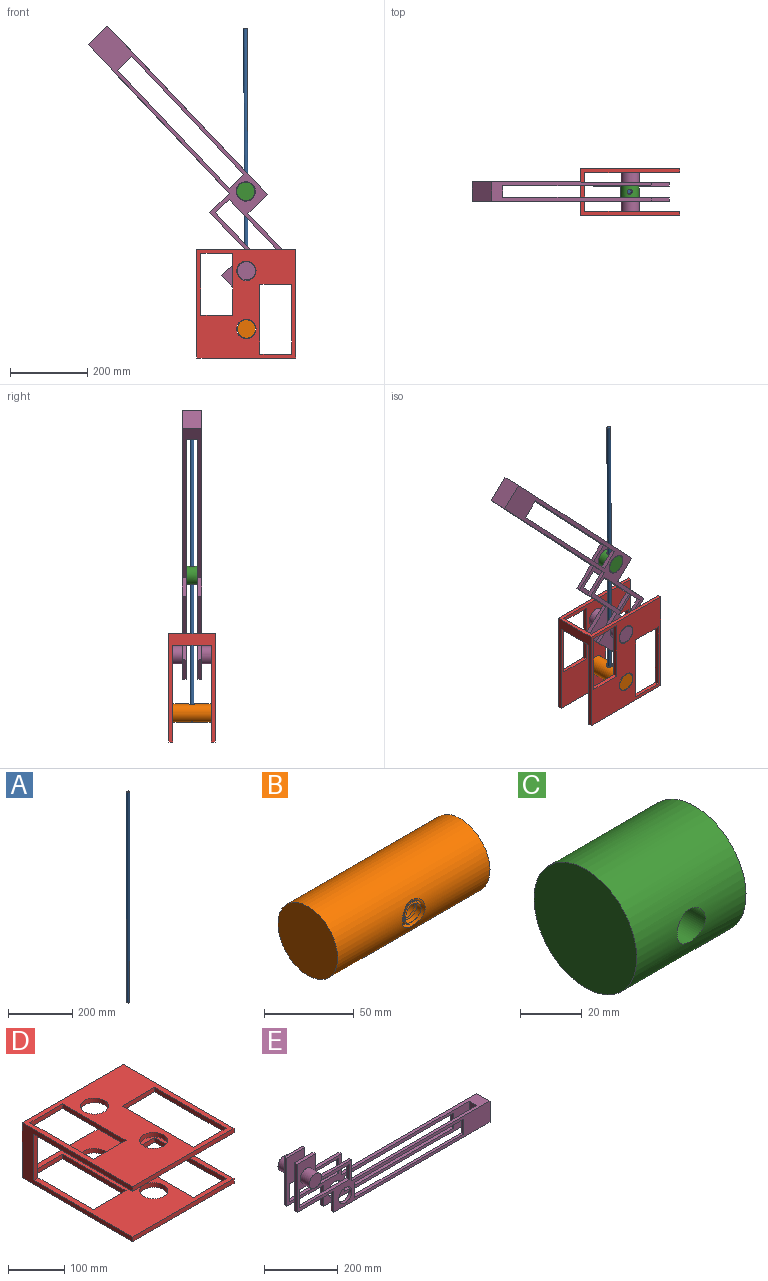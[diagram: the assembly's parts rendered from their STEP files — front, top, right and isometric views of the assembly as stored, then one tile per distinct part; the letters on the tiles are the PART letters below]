
ASSEMBLY  parts=5 mates=5
PART A: 3 faces, bbox 10x10x800 mm
  f0: cylinder r=5mm len=800mm, axis (0,0,-1), area 25132.7mm2, adj f1,f2
  f1: plane 10x10mm, normal (0,0,1), area 78.5mm2, adj f0
  f2: plane 10x10mm, normal (0,0,-1), area 78.5mm2, adj f0
PART B: 18 faces, bbox 120x48.7x47 mm
  f0: cylinder r=23.5mm len=120mm, axis (-1,0,0), area 17326.1mm2, adj f1,f11,f12,f13
  f1: cylinder r=6.5mm len=13mm, axis (0,1,0), area 373.7mm2, adj f0,f2,f14,f15,f16
  f2: cylinder r=6.5mm len=13mm, axis (0,1,0), area 132.8mm2, adj f1,f3,f15,f16
  f3: cylinder r=6.5mm len=13mm, axis (0,1,0), area 132.8mm2, adj f2,f4,f15,f16
  f4: cylinder r=6.5mm len=13mm, axis (0,1,0), area 132.8mm2, adj f3,f5,f15,f16
  f5: cylinder r=6.5mm len=13mm, axis (0,1,0), area 132.8mm2, adj f4,f6,f15,f16
  f6: cylinder r=6.5mm len=13mm, axis (0,1,0), area 132.8mm2, adj f5,f7,f15,f16
  f7: cylinder r=6.5mm len=13mm, axis (0,1,0), area 132.8mm2, adj f6,f8,f15,f16
  f8: cylinder r=6.5mm len=13mm, axis (0,1,0), area 129.1mm2, adj f7,f9,f10,f15,f16
  f9: cylinder r=6.5mm len=12.36mm, axis (0,1,0), area 17.2mm2, adj f8,f10,f16
  f10: cylinder r=23.5mm len=13.46mm, axis (-1,0,0), area 23.3mm2, adj f8,f9,f15,f16
  f11: plane 47x47mm, normal (1,0,0), area 1734.9mm2, adj f0
  f12: plane 47x47mm, normal (-1,0,0), area 1734.9mm2, adj f0
  f13: cylinder r=8.98mm len=41.22mm, axis (0,1,0), area 2185.7mm2, adj f0,f14,f17
  f14: plane 6.01x3.66mm, normal (0.6,0,0.8), area 18.2mm2, adj f1,f13,f15,f16,f17
  f15: bspline ~42.41x15.26mm, area 691mm2, adj f1,f2,f3,f4,f5,f6,f7,f8
  f16: bspline ~41.67x17.79mm, area 766.8mm2, adj f1,f2,f3,f4,f5,f6,f7,f8
  f17: bspline ~20.58x19.11mm, area 77mm2, adj f13,f14,f15
PART C: 4 faces, bbox 50x47x47 mm
  f0: cylinder r=23.5mm len=50mm, axis (1,0,0), area 7114.4mm2, adj f1,f2,f3
  f1: plane 47x47mm, normal (-1,0,0), area 1734.9mm2, adj f0
  f2: cylinder r=6.5mm len=47mm, axis (0,1,0), area 1882.3mm2, adj f0
  f3: plane 47x47mm, normal (1,0,0), area 1734.9mm2, adj f0
PART D: 32 faces, bbox 255x280x120 mm
  f0: plane 280x255mm, normal (0,0,1), area 39423mm2, adj f4,f5,f6,f7,f11,f12,f16,f17
  f1: plane 280x255mm, normal (0,0,-1), area 39423mm2, adj f6,f7,f8,f9,f13,f14,f24,f25
  f2: plane 280x255mm, normal (0,0,1), area 39129mm2, adj f6,f7,f8,f9,f10,f13,f14,f15
  f3: plane 280x255mm, normal (0,0,-1), area 39129mm2, adj f4,f5,f6,f7,f10,f11,f12,f15
  f4: plane 255x10mm, normal (0,-1,0), area 2550mm2, adj f0,f3,f5,f7
  f5: plane 280x10mm, normal (1,0,0), area 2800mm2, adj f0,f3,f4,f6
  f6: plane 255x120mm, normal (0,1,0), area 6080mm2, adj f0,f1,f2,f3,f5,f7,f9,f10
  f7: plane 280x120mm, normal (-1,0,0), area 8600mm2, adj f0,f1,f2,f3,f4,f6,f8,f15
  f8: plane 255x10mm, normal (0,-1,0), area 2550mm2, adj f1,f2,f7,f9
  f9: plane 280x10mm, normal (1,0,0), area 2800mm2, adj f1,f2,f6,f8
  f10: plane 100x30mm, normal (1,0,0), area 3000mm2, adj f2,f3,f6,f15
  f11: cylinder r=25mm len=50mm, axis (0,0,1), area 1570.8mm2, adj f0,f3
  f12: cylinder r=25mm len=50mm, axis (0,0,1), area 1570.8mm2, adj f0,f3
  f13: cylinder r=25mm len=50mm, axis (0,0,1), area 1570.8mm2, adj f1,f2
  f14: cylinder r=25mm len=50mm, axis (0,0,1), area 1570.8mm2, adj f1,f2
  f15: plane 100x9.8mm, normal (0,-1,0), area 980mm2, adj f2,f3,f7,f10
  f16: plane 180x10mm, normal (1,0,0), area 1800mm2, adj f0,f3,f17,f19
  f17: plane 82.5x10mm, normal (0,-1,0), area 825mm2, adj f0,f3,f16,f18
  f18: plane 180x10mm, normal (-1,0,0), area 1800mm2, adj f0,f3,f17,f19
  f19: plane 82.5x10mm, normal (0,1,0), area 825mm2, adj f0,f3,f16,f18
  f20: plane 160x10mm, normal (-1,0,0), area 1600mm2, adj f0,f3,f21,f23
  f21: plane 82.5x10mm, normal (0,1,0), area 825mm2, adj f0,f3,f20,f22
  f22: plane 160x10mm, normal (1,0,0), area 1600mm2, adj f0,f3,f21,f23
  f23: plane 82.5x10mm, normal (0,-1,0), area 825mm2, adj f0,f3,f20,f22
  f24: plane 82.5x10mm, normal (0,1,0), area 825mm2, adj f1,f2,f25,f27
  f25: plane 180x10mm, normal (-1,0,0), area 1800mm2, adj f1,f2,f24,f26
  f26: plane 82.5x10mm, normal (0,-1,0), area 825mm2, adj f1,f2,f25,f27
  f27: plane 180x10mm, normal (1,0,0), area 1800mm2, adj f1,f2,f24,f26
  f28: plane 82.5x10mm, normal (0,-1,0), area 825mm2, adj f1,f2,f29,f31
  f29: plane 160x10mm, normal (1,0,0), area 1600mm2, adj f1,f2,f28,f30
  f30: plane 82.5x10mm, normal (0,1,0), area 825mm2, adj f1,f2,f29,f31
  f31: plane 160x10mm, normal (-1,0,0), area 1600mm2, adj f1,f2,f28,f30
PART E: 48 faces, bbox 740x120x230 mm
  f0: plane 740x230mm, normal (0,-1,0), area 28301.6mm2, adj f4,f6,f9,f13,f15,f16,f17,f18
  f1: plane 740x230mm, normal (0,1,0), area 28301.6mm2, adj f5,f7,f8,f9,f10,f11,f12,f14
  f2: plane 700x230mm, normal (0,-1,0), area 27236.5mm2, adj f5,f7,f8,f9,f10,f11,f12,f14
  f3: plane 700x230mm, normal (0,1,0), area 27236.5mm2, adj f4,f6,f9,f13,f15,f16,f18,f19
  f4: plane 70x10mm, normal (-1,0,0), area 700mm2, adj f0,f3,f15,f16
  f5: plane 70x10mm, normal (0,0,1), area 700mm2, adj f1,f2,f12,f14
  f6: plane 160x10mm, normal (-1,0,0), area 1600mm2, adj f0,f3,f13,f15
  f7: plane 140x10mm, normal (0,0,-1), area 1400mm2, adj f1,f2,f8,f14
  f8: plane 70x10mm, normal (-1,0,0), area 700mm2, adj f1,f2,f7,f16
  f9: plane 530x50mm, normal (0,0,1), area 11800mm2, adj f0,f1,f2,f3,f10,f17,f18,f25
  f10: plane 70x10mm, normal (1,0,0), area 700mm2, adj f1,f2,f9,f11
  f11: plane 140x10mm, normal (0,0,1), area 1400mm2, adj f1,f2,f10,f12
  f12: plane 90x10mm, normal (1,0,0), area 900mm2, adj f1,f2,f5,f11
  f13: plane 70x10mm, normal (0,0,1), area 700mm2, adj f0,f3,f6,f20
  f14: plane 160x10mm, normal (-1,0,0), area 1600mm2, adj f1,f2,f5,f7
  f15: plane 140x10mm, normal (0,0,-1), area 1400mm2, adj f0,f3,f4,f6
  f16: plane 600x50mm, normal (0,0,-1), area 13200mm2, adj f0,f1,f2,f3,f4,f8,f17,f25
  f17: plane 70x50mm, normal (1,0,0), area 3500mm2, adj f0,f1,f9,f16
  f18: plane 70x10mm, normal (1,0,0), area 700mm2, adj f0,f3,f9,f19
  f19: plane 140x10mm, normal (0,0,1), area 1400mm2, adj f0,f3,f18,f20
  f20: plane 90x10mm, normal (1,0,0), area 900mm2, adj f0,f3,f13,f19
  f21: cylinder r=23.5mm len=47mm, axis (0,1,0), area 5167.9mm2, adj f0,f22
  f22: plane 47x47mm, normal (0,-1,0), area 1734.9mm2, adj f21
  f23: cylinder r=23.5mm len=47mm, axis (0,-1,0), area 5167.9mm2, adj f1,f24
  f24: plane 47x47mm, normal (0,1,0), area 1734.9mm2, adj f23
  f25: plane 70x30mm, normal (-1,0,0), area 2100mm2, adj f2,f3,f9,f16
  f26: cylinder r=25mm len=50mm, axis (0,-1,0), area 1570.8mm2, adj f0,f3
  f27: cylinder r=25mm len=50mm, axis (0,-1,0), area 1570.8mm2, adj f1,f2
  f28: plane 60x10mm, normal (1,0,0), area 600mm2, adj f0,f3,f29,f33
  f29: plane 50x10mm, normal (0,0,-1), area 500mm2, adj f0,f3,f28,f30
  f30: plane 10x10mm, normal (-1,0,0), area 100mm2, adj f0,f3,f29,f31
  f31: plane 140x10mm, normal (0,0,-1), area 1400mm2, adj f0,f3,f30,f32
  f32: plane 50x10mm, normal (-1,0,0), area 500mm2, adj f0,f3,f31,f33
  f33: plane 190x10mm, normal (0,0,1), area 1900mm2, adj f0,f3,f28,f32
  f34: plane 50x10mm, normal (-1,0,0), area 500mm2, adj f0,f3,f35,f37
  f35: plane 420x10mm, normal (0,0,1), area 4200mm2, adj f0,f3,f34,f36
  f36: plane 50x10mm, normal (1,0,0), area 500mm2, adj f0,f3,f35,f37
  f37: plane 420x10mm, normal (0,0,-1), area 4200mm2, adj f0,f3,f34,f36
  f38: plane 190x10mm, normal (0,0,1), area 1900mm2, adj f1,f2,f39,f43
  f39: plane 50x10mm, normal (-1,0,0), area 500mm2, adj f1,f2,f38,f40
  f40: plane 140x10mm, normal (0,0,-1), area 1400mm2, adj f1,f2,f39,f41
  f41: plane 10x10mm, normal (-1,0,0), area 100mm2, adj f1,f2,f40,f42
  f42: plane 50x10mm, normal (0,0,-1), area 500mm2, adj f1,f2,f41,f43
  f43: plane 60x10mm, normal (1,0,0), area 600mm2, adj f1,f2,f38,f42
  f44: plane 420x10mm, normal (0,0,-1), area 4200mm2, adj f1,f2,f45,f47
  f45: plane 50x10mm, normal (1,0,0), area 500mm2, adj f1,f2,f44,f46
  f46: plane 420x10mm, normal (0,0,1), area 4200mm2, adj f1,f2,f45,f47
  f47: plane 50x10mm, normal (-1,0,0), area 500mm2, adj f1,f2,f44,f46
PLACE A rot(axis=(0,-1,0),0.2deg) t=(48.23,260.66,-57.77)mm
PLACE B rot(axis=(-0.58,-0.58,0.58),120.1deg) t=(98.6,210.66,-153.78)mm
PLACE C rot(axis=(-0.58,-0.58,0.58),120.1deg) t=(107.36,235.66,171.43)mm
PLACE D rot(axis=(1,0,0),90deg) t=(-79.36,320.66,-108.98)mm fixed
PLACE E rot(axis=(0,-1,0),133.4deg) t=(199.33,285.66,210.85)mm
MATE revolute B.f0 <-> D.f12  axis (0,-1,0) through (48.14,200.66,-33.98)mm
MATE revolute A.f0 <-> B.f1  axis (0,0,-1) through (48.23,260.66,-57.77)mm
MATE revolute C.f0 <-> E.f26  axis (0,-1,0) through (46.78,235.66,321.2)mm
MATE revolute E.f21 <-> D.f11  axis (0,-1,0) through (48.14,200.66,116.02)mm
MATE slider A.f0 <-> C.f2  axis (0,0,-1) through (46.7,260.66,342.23)mm
